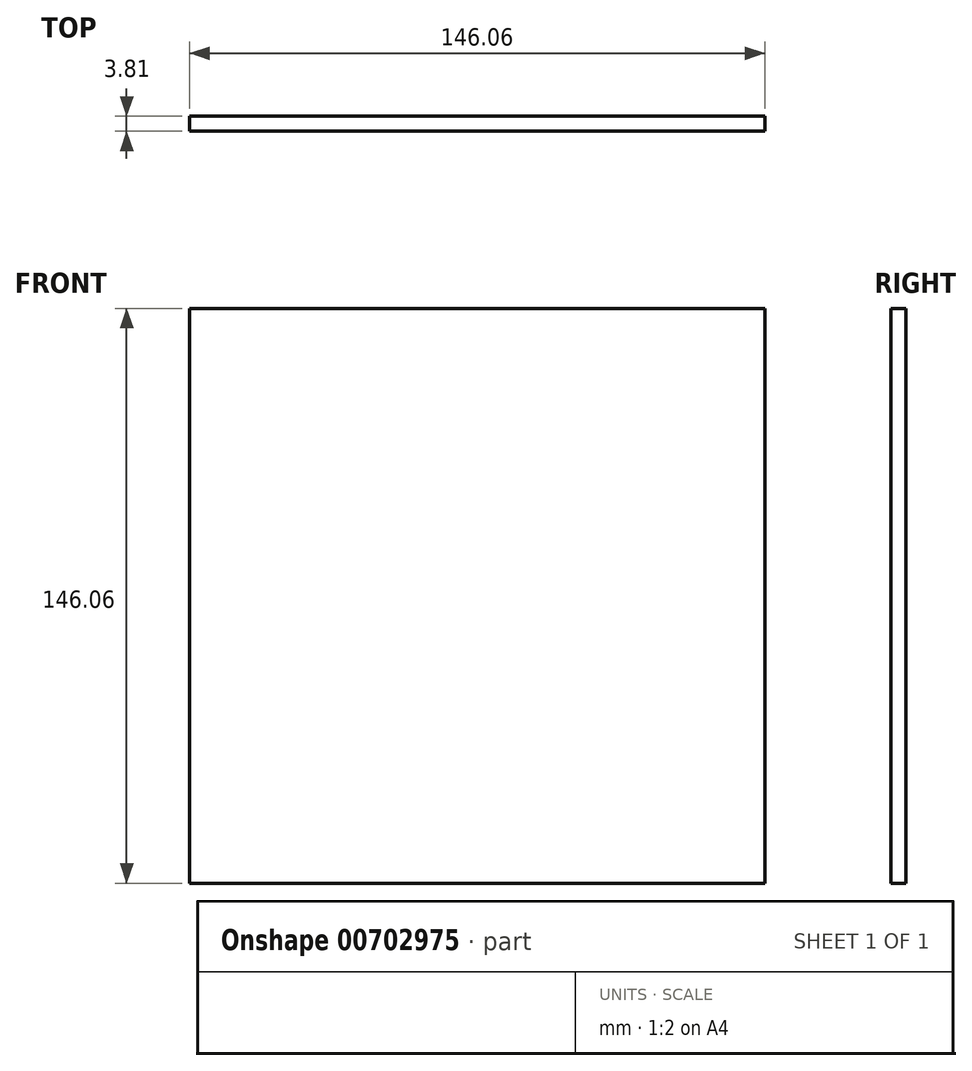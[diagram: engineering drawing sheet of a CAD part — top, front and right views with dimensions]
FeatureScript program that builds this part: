
annotation { "Feature Type Name" : "Feature", "Feature Type Description" : "" }
export const myFeature = defineFeature(function(context is Context, id is Id, definition is map)
    precondition{}
    {
        {
            var Q0;
            Q0=qCreatedBy(makeId("Front.planeOp"),FACE);
            var sketch = newSketch(context, id + "F0", { "sketchPlane" : qUnion([Q0])});
            skLineSegment(sketch, "E0.bottom", {"start": v(76.2, 76.2) * mm, "end": v(-76.2, 76.2) * mm, "construction": true});
            skLineSegment(sketch, "E0.top", {"start": v(76.2, -76.2) * mm, "end": v(-76.2, -76.2) * mm, "construction": true});
            skLineSegment(sketch, "E0.left", {"start": v(76.2, 76.2) * mm, "end": v(76.2, -76.2) * mm, "construction": true});
            skLineSegment(sketch, "E0.right", {"start": v(-76.2, 76.2) * mm, "end": v(-76.2, -76.2) * mm, "construction": true});
            skPoint(sketch, "E0.middle", {"position": v(0, 0) * mm});
            skLineSegment(sketch, "E1.bottom", {"start": v(73.02, 73.02) * mm, "end": v(-73.03, 73.02) * mm});
            skLineSegment(sketch, "E1.top", {"start": v(73.03, -73.02) * mm, "end": v(-73.02, -73.02) * mm});
            skLineSegment(sketch, "E1.left", {"start": v(73.03, 73.03) * mm, "end": v(73.03, -73.02) * mm});
            skLineSegment(sketch, "E1.right", {"start": v(-73.03, 73.02) * mm, "end": v(-73.03, -73.03) * mm});
            skSolve(sketch);
        }
        {
            var Q0;
            Q0 = qSketchRegion(id + "F0", true);
            extrude(context, id + "F1", {"entities" : qUnion([Q0]), "depth" : 3.8 * mm, "offsetDistance" : 25.4 * mm});
        }
    });
